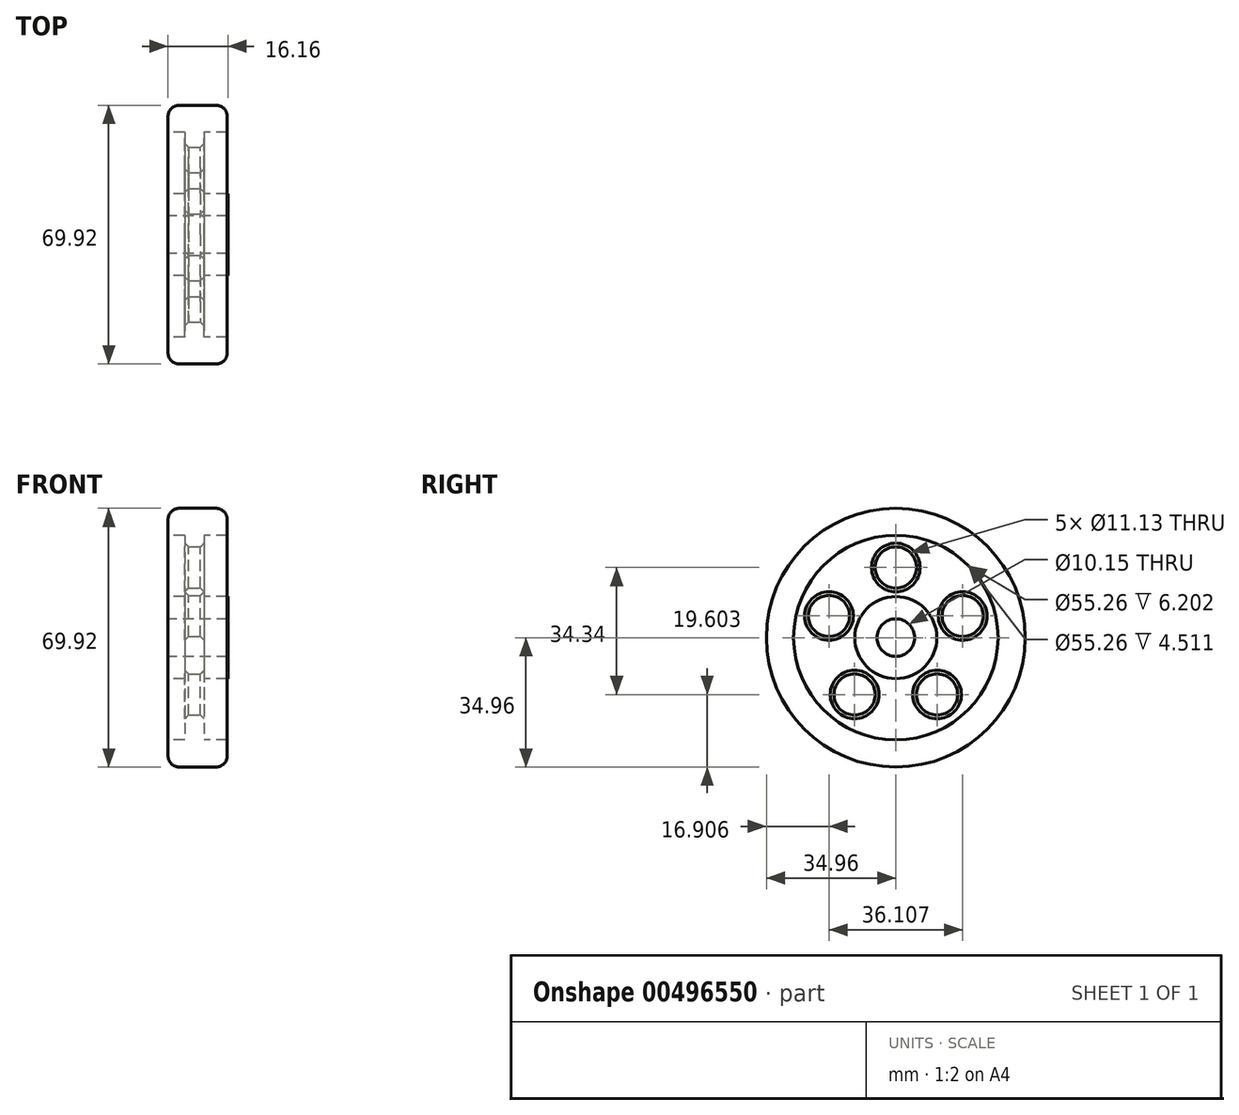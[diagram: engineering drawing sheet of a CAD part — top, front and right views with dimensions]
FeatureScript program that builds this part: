
annotation { "Feature Type Name" : "Feature", "Feature Type Description" : "" }
export const myFeature = defineFeature(function(context is Context, id is Id, definition is map)
    precondition{}
    {
        {
            var Q0;
            Q0=qCreatedBy(makeId("Front.planeOp"),FACE);
            var sketch = newSketch(context, id + "F0", { "sketchPlane" : qUnion([Q0])});
            skLineSegment(sketch, "E0", {"start": v(0, 5.07) * mm, "end": v(16.16, 5.07) * mm});
            skLineSegment(sketch, "E1", {"start": v(16.16, 5.07) * mm, "end": v(16.16, 11.09) * mm});
            skLineSegment(sketch, "E2", {"start": v(16.16, 11.09) * mm, "end": v(9.77, 11.09) * mm});
            skLineSegment(sketch, "E3", {"start": v(9.77, 11.09) * mm, "end": v(9.77, 27.63) * mm});
            skLineSegment(sketch, "E4", {"start": v(9.77, 27.63) * mm, "end": v(15.98, 27.63) * mm});
            skLineSegment(sketch, "E5", {"start": v(15.98, 27.63) * mm, "end": v(15.98, 34.96) * mm});
            skLineSegment(sketch, "E6", {"start": v(15.98, 34.96) * mm, "end": v(0, 34.96) * mm});
            skLineSegment(sketch, "E7", {"start": v(0, 34.96) * mm, "end": v(0, 27.63) * mm});
            skLineSegment(sketch, "E8", {"start": v(0, 27.63) * mm, "end": v(4.51, 27.63) * mm});
            skLineSegment(sketch, "E9", {"start": v(4.51, 27.63) * mm, "end": v(4.51, 11.09) * mm});
            skLineSegment(sketch, "E10", {"start": v(4.51, 11.09) * mm, "end": v(0, 11.09) * mm});
            skLineSegment(sketch, "E11", {"start": v(0, 11.09) * mm, "end": v(0, 5.07) * mm});
            skLineSegment(sketch, "E12", {"start": v(0, 0) * mm, "end": v(37.78, 0) * mm});
            skSolve(sketch);
        }
        {
            var Q0;
            Q0=makeQuery(id+"F0.imprint","IMPRINT",FACE,{"disambiguationData":[TD([[makeQuery(id+"F0.imprint","IMPRINT",EDGE,{"derivedFrom":sQuery(id+"F0.wireOp",EDGE,"E0")}),1.0]])]});
            var Q1;
            Q1=sQuery(id+"F0.wireOp",EDGE,"E12");
            revolve(context, id + "F1", {"entities" : qUnion([Q0]), "axis" : qUnion([Q1]), "revolveType" : RevolveType.FULL});
        }
        {
            var Q0;
            Q0=makeQuery(id+"F1.opRevolve","SWEPT_FACE",FACE,{"disambiguationData":[OSD([sQuery(id+"F0.wireOp",EDGE,"E3")])]});
            var sketch = newSketch(context, id + "F2", { "sketchPlane" : qUnion([Q0])});
            skCircle(sketch, "E13", {"center": v(0, 18.98) * mm, "radius": 5.57 * mm});
            skCircle(sketch, "E14.1.0", {"center": v(-18.05, 5.87) * mm, "radius": 5.57 * mm});
            skCircle(sketch, "E14.2.0", {"center": v(-11.16, -15.36) * mm, "radius": 5.57 * mm});
            skCircle(sketch, "E14.3.0", {"center": v(11.16, -15.36) * mm, "radius": 5.57 * mm});
            skCircle(sketch, "E14.4.0", {"center": v(18.05, 5.87) * mm, "radius": 5.57 * mm});
            skPoint(sketch, "E14.center", {"position": v(0, 0) * mm});
            skSolve(sketch);
        }
        {
            var Q0;
            Q0=makeQuery(id+"F2.imprint","IMPRINT",FACE,{"disambiguationData":[TD([[makeQuery(id+"F2.imprint","IMPRINT",EDGE,{"derivedFrom":sQuery(id+"F2.wireOp",EDGE,"E13")}),1.0]])]});
            var Q1;
            Q1=makeQuery(id+"F2.imprint","IMPRINT",FACE,{"disambiguationData":[TD([[makeQuery(id+"F2.imprint","IMPRINT",EDGE,{"derivedFrom":sQuery(id+"F2.wireOp",EDGE,"E14.4.0")}),1.0]])]});
            var Q2;
            Q2=makeQuery(id+"F2.imprint","IMPRINT",FACE,{"disambiguationData":[TD([[makeQuery(id+"F2.imprint","IMPRINT",EDGE,{"derivedFrom":sQuery(id+"F2.wireOp",EDGE,"E14.3.0")}),1.0]])]});
            var Q3;
            Q3=makeQuery(id+"F2.imprint","IMPRINT",FACE,{"disambiguationData":[TD([[makeQuery(id+"F2.imprint","IMPRINT",EDGE,{"derivedFrom":sQuery(id+"F2.wireOp",EDGE,"E14.1.0")}),1.0]])]});
            var Q4;
            Q4=makeQuery(id+"F2.imprint","IMPRINT",FACE,{"disambiguationData":[TD([[makeQuery(id+"F2.imprint","IMPRINT",EDGE,{"derivedFrom":sQuery(id+"F2.wireOp",EDGE,"E14.2.0")}),1.0]])]});
            extrude(context, id + "F3", {"entities" : qUnion([Q0, Q1, Q2, Q3, Q4]), "operationType" : NewBodyOperationType.REMOVE, "oppositeDirection" : true, "depth" : 25 * mm});
        }
        {
            var Q0;
            Q0=makeQuery(id+"F1.opRevolve","SWEPT_EDGE",EDGE,{"disambiguationData":[OSD([sQuery(id+"F0.wireOp",EDGE,"E5"),sQuery(id+"F0.wireOp",EDGE,"E6")])]});
            var Q1;
            Q1=makeQuery(id+"F1.opRevolve","SWEPT_EDGE",EDGE,{"disambiguationData":[OSD([sQuery(id+"F0.wireOp",EDGE,"E6"),sQuery(id+"F0.wireOp",EDGE,"E7")])]});
            fillet(context, id + "F4", {"entities" : qUnion([Q0, Q1]), "radius" : 3 * mm, "tangentPropagation" : true, "allowEdgeOverflow" : false});
        }
        {
            var Q0;
            Q0=makeQuery(id+"F3.boolean.opBoolean","COPY",EDGE,{"derivedFrom":makeQuery(id+"F3.opExtrude","CAP_EDGE",EDGE,{"disambiguationData":[OSD([sQuery(id+"F2.wireOp",EDGE,"E14.4.0")])],"isStart":true})});
            var Q1;
            Q1=makeQuery(id+"F3.boolean.opBoolean","COPY",FACE,{"derivedFrom":makeQuery(id+"F3.opExtrude","SWEPT_FACE",FACE,{"disambiguationData":[OSD([sQuery(id+"F2.wireOp",EDGE,"E13")])]})});
            var Q2;
            Q2=makeQuery(id+"F3.boolean.opBoolean","COPY",FACE,{"derivedFrom":makeQuery(id+"F3.opExtrude","SWEPT_FACE",FACE,{"disambiguationData":[OSD([sQuery(id+"F2.wireOp",EDGE,"E14.1.0")])]})});
            var Q3;
            Q3=makeQuery(id+"F3.boolean.opBoolean","COPY",FACE,{"derivedFrom":makeQuery(id+"F3.opExtrude","SWEPT_FACE",FACE,{"disambiguationData":[OSD([sQuery(id+"F2.wireOp",EDGE,"E14.2.0")])]})});
            var Q4;
            Q4=makeQuery(id+"F3.boolean.opBoolean","COPY",FACE,{"derivedFrom":makeQuery(id+"F3.opExtrude","SWEPT_FACE",FACE,{"disambiguationData":[OSD([sQuery(id+"F2.wireOp",EDGE,"E14.3.0")])]})});
            var Q5;
            Q5=makeQuery(id+"F3.boolean.opBoolean","COPY",FACE,{"derivedFrom":makeQuery(id+"F3.opExtrude","SWEPT_FACE",FACE,{"disambiguationData":[OSD([sQuery(id+"F2.wireOp",EDGE,"E14.4.0")])]})});
            chamfer(context, id + "F5", {"entities" : qUnion([Q0, Q1, Q2, Q3, Q4, Q5]), "width" : 1 * mm, "tangentPropagation" : true});
        }
    });
